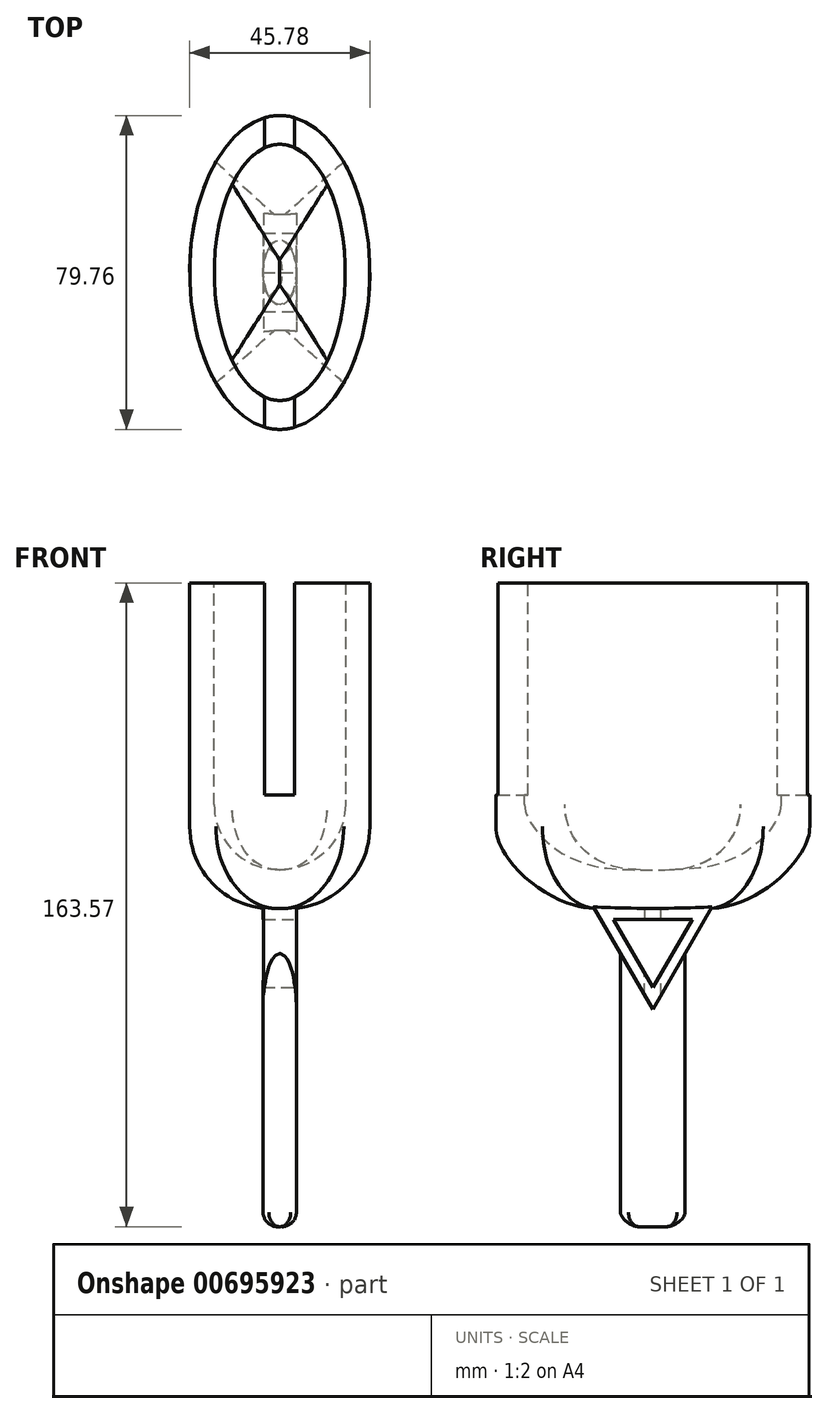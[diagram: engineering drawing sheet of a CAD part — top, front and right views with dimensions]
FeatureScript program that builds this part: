
annotation { "Feature Type Name" : "Feature", "Feature Type Description" : "" }
export const myFeature = defineFeature(function(context is Context, id is Id, definition is map)
    precondition{}
    {
        {
            var Q0;
            Q0=qCreatedBy(makeId("Top.planeOp"),FACE);
            var sketch = newSketch(context, id + "F0", { "sketchPlane" : qUnion([Q0])});
            skEllipse(sketch, "E0", {"center": v(0, 0) * mm, "majorRadius": 39.88 * mm, "minorRadius": 22.9 * mm, "majorAxis": v(0, -1)});
            skSolve(sketch);
        }
        {
            var Q0;
            Q0=makeQuery(id+"F0.imprint","IMPRINT",FACE,{"disambiguationData":[TD([[makeQuery(id+"F0.imprint","IMPRINT",EDGE,{"derivedFrom":sQuery(id+"F0.wireOp",EDGE,"E0")}),1.0]])]});
            extrude(context, id + "F1", {"entities" : qUnion([Q0]), "depth" : 48.5 * mm, "offsetDistance" : 25.4 * mm});
        }
        {
            var Q0;
            Q0=makeQuery(id+"F1.opExtrude","CAP_FACE",FACE,{"disambiguationData":[OSD([sQuery(id+"F0.wireOp",EDGE,"E0")])],"isStart":true});
            extrude(context, id + "F2", {"entities" : qUnion([Q0]), "operationType" : NewBodyOperationType.ADD, "depth" : 34.3 * mm, "offsetDistance" : 25.4 * mm});
        }
        {
            var Q0;
            Q0=makeQuery(id+"F2.opExtrude","CAP_EDGE",EDGE,{"disambiguationData":[OSD([sQuery(id+"F0.wireOp",EDGE,"E0")])],"isStart":false});
            fillet(context, id + "F3", {"entities" : qUnion([Q0]), "radius" : 20.85 * mm, "tangentPropagation" : true, "allowEdgeOverflow" : false});
        }
        {
            var Q0;
            Q0=qCreatedBy(makeId("Right.planeOp"),FACE);
            var sketch = newSketch(context, id + "F4", { "sketchPlane" : qUnion([Q0])});
            skCircle(sketch, "E1.cCircle", {"center": v(0, -34.7) * mm, "radius": 12.55 * mm, "construction": true});
            skLineSegment(sketch, "E1.0", {"start": v(-21.74, -22.16) * mm, "end": v(21.74, -22.16) * mm});
            skLineSegment(sketch, "E1.1", {"start": v(21.74, -22.16) * mm, "end": v(0, -59.81) * mm});
            skLineSegment(sketch, "E1.2", {"start": v(0, -59.81) * mm, "end": v(-21.74, -22.16) * mm});
            skPoint(sketch, "E1.0.midPoint", {"position": v(0, -22.16) * mm});
            skSolve(sketch);
        }
        {
            var Q0;
            Q0 = qSketchRegion(id + "F4", true);
            extrude(context, id + "F5", {"entities" : qUnion([Q0]), "operationType" : NewBodyOperationType.ADD, "depth" : 4.32 * mm, "offsetDistance" : 25.4 * mm});
        }
        {
            var Q0;
            Q0=makeQuery(id+"F5.opExtrude","CAP_FACE",FACE,{"disambiguationData":[OSD([sQuery(id+"F4.wireOp",EDGE,"E1.0"),sQuery(id+"F4.wireOp",EDGE,"E1.1"),sQuery(id+"F4.wireOp",EDGE,"E1.2")])],"isStart":false});
            extrude(context, id + "F6", {"entities" : qUnion([Q0]), "operationType" : NewBodyOperationType.ADD, "oppositeDirection" : true, "depth" : 8.4 * mm, "offsetDistance" : 25.4 * mm});
        }
        {
            var Q0;
            Q0=makeQuery(id+"F1.opExtrude","CAP_FACE",FACE,{"disambiguationData":[OSD([sQuery(id+"F0.wireOp",EDGE,"E0")])],"isStart":false});
            var sketch = newSketch(context, id + "F7", { "sketchPlane" : qUnion([Q0])});
            skEllipse(sketch, "E2", {"center": v(0, 0) * mm, "majorRadius": 8.2 * mm, "minorRadius": 4.23 * mm, "majorAxis": v(0, 1)});
            skSolve(sketch);
        }
        {
            var Q0;
            Q0 = qSketchRegion(id + "F7", true);
            extrude(context, id + "F8", {"entities" : qUnion([Q0]), "operationType" : NewBodyOperationType.ADD, "oppositeDirection" : true, "depth" : 163.58 * mm, "offsetDistance" : 25.4 * mm});
        }
        {
            var Q0;
            Q0=makeQuery(id+"F8.opExtrude","CAP_EDGE",EDGE,{"disambiguationData":[OSD([sQuery(id+"F7.wireOp",EDGE,"E2")])],"isStart":false});
            fillet(context, id + "F9", {"entities" : qUnion([Q0]), "radius" : 3.68 * mm, "tangentPropagation" : true, "allowEdgeOverflow" : false});
        }
        {
            var Q0;
            Q0=makeQuery(id+"F1.opExtrude","CAP_FACE",FACE,{"disambiguationData":[OSD([sQuery(id+"F0.wireOp",EDGE,"E0")])],"isStart":false});
            var sketch = newSketch(context, id + "F10", { "sketchPlane" : qUnion([Q0])});
            skEllipse(sketch, "E3", {"center": v(0, 0) * mm, "majorRadius": 32.54 * mm, "minorRadius": 16.66 * mm, "majorAxis": v(0, -1)});
            skSolve(sketch);
        }
        {
            var Q0;
            Q0 = qSketchRegion(id + "F10", true);
            extrude(context, id + "F11", {"entities" : qUnion([Q0]), "operationType" : NewBodyOperationType.REMOVE, "oppositeDirection" : true, "depth" : 72.9 * mm, "offsetDistance" : 25.4 * mm});
        }
        {
            var Q0;
            Q0=makeQuery(id+"F11.boolean.opBoolean","COPY",EDGE,{"derivedFrom":makeQuery(id+"F11.opExtrude","CAP_EDGE",EDGE,{"disambiguationData":[OSD([sQuery(id+"F10.wireOp",EDGE,"E3")])],"isStart":false})});
            fillet(context, id + "F12", {"entities" : qUnion([Q0]), "radius" : 16.56 * mm, "tangentPropagation" : true, "allowEdgeOverflow" : false});
        }
        {
            var Q0;
            Q0=qCreatedBy(makeId("Right.planeOp"),FACE);
            var sketch = newSketch(context, id + "F13", { "sketchPlane" : qUnion([Q0])});
            skLineSegment(sketch, "E4.bottom", {"start": v(-49.17, -5.44) * mm, "end": v(49.17, -5.44) * mm});
            skLineSegment(sketch, "E4.top", {"start": v(-49.17, 68.6) * mm, "end": v(49.17, 68.6) * mm});
            skLineSegment(sketch, "E4.left", {"start": v(-49.17, -5.44) * mm, "end": v(-49.17, 68.6) * mm});
            skLineSegment(sketch, "E4.right", {"start": v(49.17, -5.44) * mm, "end": v(49.17, 68.6) * mm});
            skPoint(sketch, "E4.middle", {"position": v(0, 31.58) * mm});
            skSolve(sketch);
        }
        {
            var Q0;
            Q0 = qSketchRegion(id + "F13", true);
            extrude(context, id + "F14", {"entities" : qUnion([Q0]), "operationType" : NewBodyOperationType.REMOVE, "oppositeDirection" : true, "depth" : 3.8 * mm, "offsetDistance" : 25.4 * mm});
        }
        {
            var Q0;
            Q0 = qSketchRegion(id + "F13", true);
            extrude(context, id + "F15", {"entities" : qUnion([Q0]), "operationType" : NewBodyOperationType.REMOVE, "depth" : 3.8 * mm, "offsetDistance" : 25.4 * mm});
        }
        {
            var Q0;
            Q0=makeQuery(id+"F5.opExtrude","CAP_FACE",FACE,{"disambiguationData":[OSD([sQuery(id+"F4.wireOp",EDGE,"E1.0"),sQuery(id+"F4.wireOp",EDGE,"E1.1"),sQuery(id+"F4.wireOp",EDGE,"E1.2")])],"isStart":false});
            var sketch = newSketch(context, id + "F16", { "sketchPlane" : qUnion([Q0])});
            skCircle(sketch, "E5.cCircle", {"center": v(0, -42.77) * mm, "radius": 11.57 * mm, "construction": true});
            skLineSegment(sketch, "E5.0", {"start": v(0, -54.34) * mm, "end": v(-10.02, -36.98) * mm});
            skLineSegment(sketch, "E5.1", {"start": v(-10.02, -36.98) * mm, "end": v(10.02, -36.98) * mm});
            skLineSegment(sketch, "E5.2", {"start": v(10.02, -36.98) * mm, "end": v(0, -54.34) * mm});
            skSolve(sketch);
        }
        {
            var Q0;
            Q0 = qSketchRegion(id + "F16", true);
            extrude(context, id + "F17", {"entities" : qUnion([Q0]), "operationType" : NewBodyOperationType.REMOVE, "oppositeDirection" : true, "depth" : 13.72 * mm, "offsetDistance" : 25.4 * mm});
        }
    });
